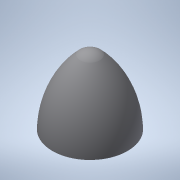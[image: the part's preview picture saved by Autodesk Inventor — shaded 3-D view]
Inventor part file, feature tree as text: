
AUTODESK INVENTOR PART (.ipt)
format: ipt  version: 2020 (Build 240168000, 168)  size: 142,848 bytes
history: native  units: mm
features: sketch x4, other x3, extrude x2, plane x1
ambient origin geometry x8: Origin, YZ Plane, XZ Plane, XY Plane, X Axis, Y Axis, Z Axis, Center Point
bodies: Body1 (feature_tree)
feature tree (10):
  other  "實體1"
  extrude  "擠出1"  Depth=21.7mm
  other  "迴轉1"
  other  "迴轉2"
  plane  "工作平面1"
  extrude  "擠出2"  Depth=18.7mm TaperAngle=0.0deg
  sketch  "草圖1"
  sketch  "草圖2"
  sketch  "草圖3"
  sketch  "草圖4"
